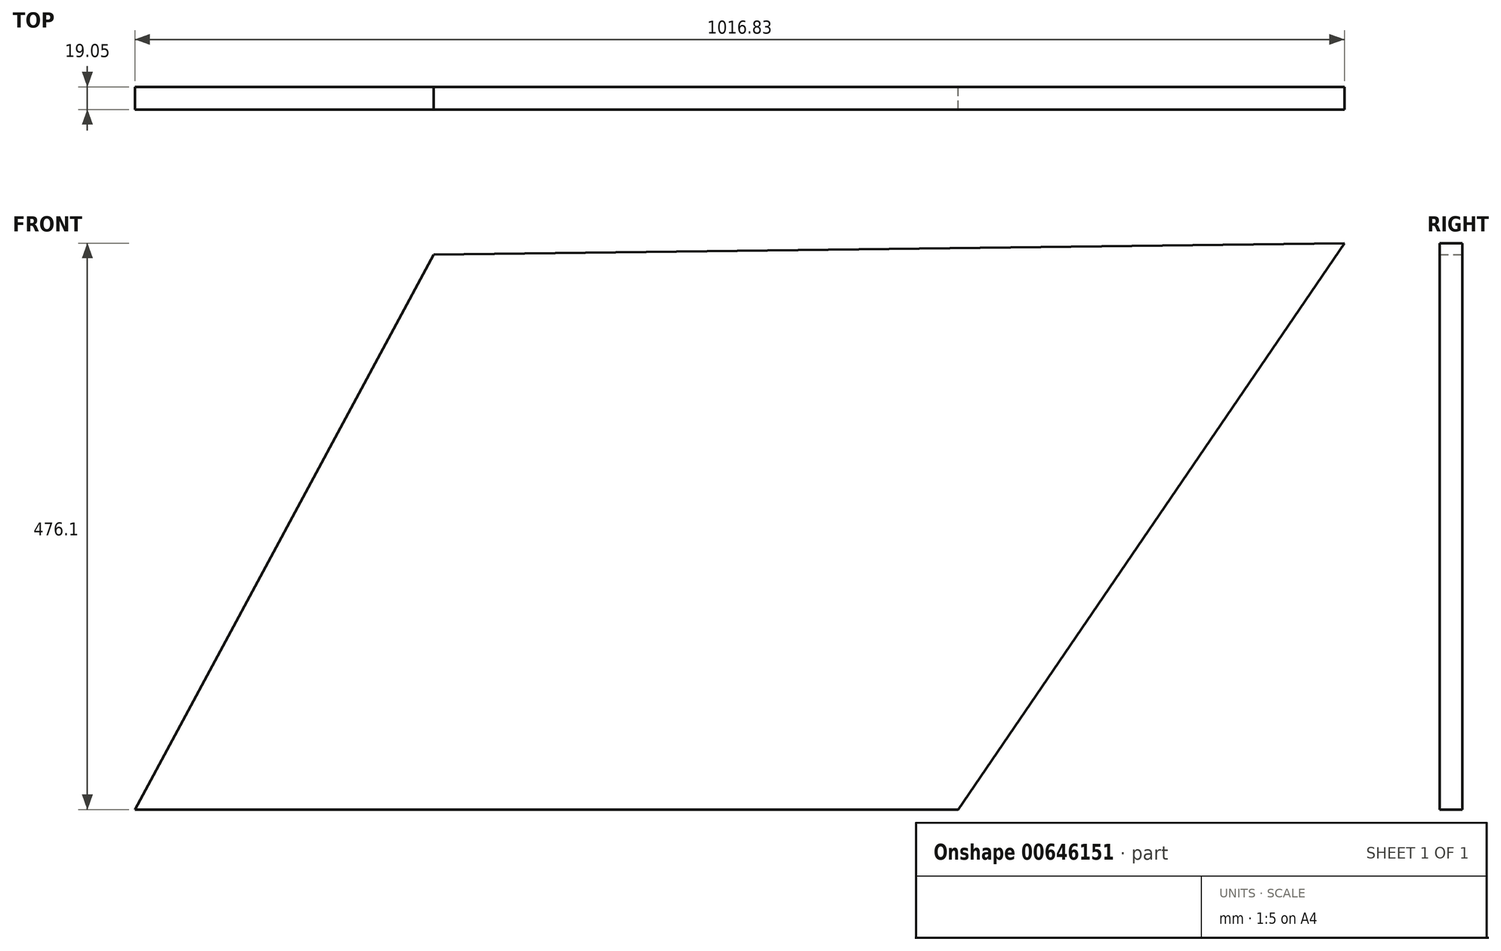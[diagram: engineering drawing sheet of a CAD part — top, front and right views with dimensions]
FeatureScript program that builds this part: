
annotation { "Feature Type Name" : "Feature", "Feature Type Description" : "" }
export const myFeature = defineFeature(function(context is Context, id is Id, definition is map)
    precondition{}
    {
        {
            var Q0;
            Q0=qCreatedBy(makeId("Front.planeOp"),FACE);
            var sketch = newSketch(context, id + "F0", { "sketchPlane" : qUnion([Q0])});
            skLineSegment(sketch, "E0", {"start": v(-241.68, 33.6) * mm, "end": v(523.97, 43.06) * mm});
            skLineSegment(sketch, "E1", {"start": v(523.97, 43.06) * mm, "end": v(199.3, -433.04) * mm});
            skLineSegment(sketch, "E2", {"start": v(199.3, -433.04) * mm, "end": v(-492.86, -433.04) * mm});
            skLineSegment(sketch, "E3", {"start": v(-492.86, -433.04) * mm, "end": v(-241.68, 33.6) * mm});
            skSolve(sketch);
        }
        {
            var Q0;
            Q0=makeQuery(id+"F0.imprint","IMPRINT",FACE,{"disambiguationData":[TD([[makeQuery(id+"F0.imprint","IMPRINT",EDGE,{"derivedFrom":sQuery(id+"F0.wireOp",EDGE,"E0")}),-1.0]])]});
            extrude(context, id + "F1", {"entities" : qUnion([Q0]), "depth" : 19.05 * mm, "offsetDistance" : 25.4 * mm});
        }
    });
